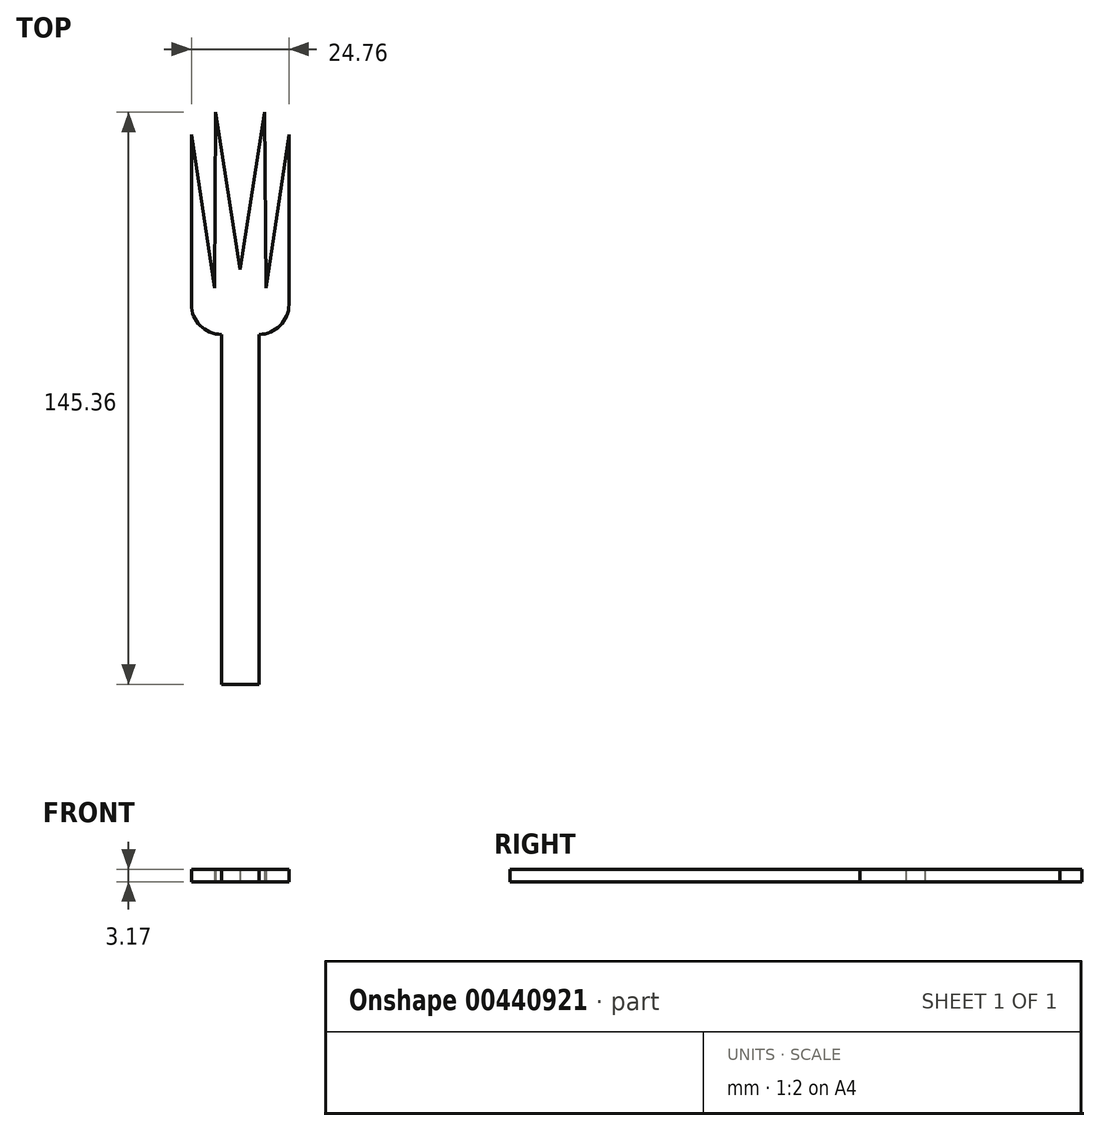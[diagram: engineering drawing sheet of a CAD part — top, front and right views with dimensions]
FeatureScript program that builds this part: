
annotation { "Feature Type Name" : "Feature", "Feature Type Description" : "" }
export const myFeature = defineFeature(function(context is Context, id is Id, definition is map)
    precondition{}
    {
        {
            var Q0;
            Q0=qCreatedBy(makeId("Top.planeOp"),FACE);
            var sketch = newSketch(context, id + "F0", { "sketchPlane" : qUnion([Q0])});
            skLineSegment(sketch, "E0.bottom", {"start": v(4.76, -44.45) * mm, "end": v(-4.76, -44.45) * mm});
            skLineSegment(sketch, "E0.left", {"start": v(4.76, -44.45) * mm, "end": v(4.76, 44.45) * mm});
            skLineSegment(sketch, "E0.right", {"start": v(-4.76, -44.45) * mm, "end": v(-4.76, 44.45) * mm});
            skPoint(sketch, "E0.middle", {"position": v(0, 0) * mm});
            skPoint(sketch, "E1.middle", {"position": v(0, 44.45) * mm});
            skLineSegment(sketch, "E2", {"start": v(4.76, 44.45) * mm, "end": v(4.76, 44.45) * mm});
            skLineSegment(sketch, "E3", {"start": v(12.38, 52.07) * mm, "end": v(12.38, 95.25) * mm});
            skLineSegment(sketch, "E4", {"start": v(12.38, 95.25) * mm, "end": v(6.52, 56.17) * mm});
            skLineSegment(sketch, "E5", {"start": v(6.52, 56.17) * mm, "end": v(6.25, 100.91) * mm});
            skLineSegment(sketch, "E6", {"start": v(6.25, 100.91) * mm, "end": v(0, 60.96) * mm});
            skLineSegment(sketch, "E7.MirrorCS", {"start": v(-6.25, 100.91) * mm, "end": v(0, 60.96) * mm});
            skLineSegment(sketch, "E8.MirrorCS", {"start": v(-6.52, 56.17) * mm, "end": v(-6.25, 100.91) * mm});
            skLineSegment(sketch, "E9.MirrorCS", {"start": v(-12.38, 95.25) * mm, "end": v(-6.52, 56.17) * mm});
            skLineSegment(sketch, "E10.MirrorCS", {"start": v(-12.38, 52.07) * mm, "end": v(-12.38, 95.25) * mm});
            skLineSegment(sketch, "E11.MirrorCS", {"start": v(-4.76, 44.45) * mm, "end": v(-4.76, 44.45) * mm});
            skPoint(sketch, "E12.visualSharp", {"position": v(-12.38, 44.45) * mm});
            skArc(sketch, "E12.filletArc", {"start": v(-12.38, 52.07) * mm, "mid": v(-10.15, 46.68) * mm, "end": v(-4.76, 44.45) * mm});
            skPoint(sketch, "E13.visualSharp", {"position": v(12.38, 44.45) * mm});
            skArc(sketch, "E13.filletArc", {"start": v(4.76, 44.45) * mm, "mid": v(10.15, 46.68) * mm, "end": v(12.38, 52.07) * mm});
            skSolve(sketch);
        }
        {
            var Q0;
            Q0 = qSketchRegion(id + "F0", true);
            extrude(context, id + "F1", {"entities" : qUnion([Q0]), "depth" : 3.17 * mm});
        }
    });
